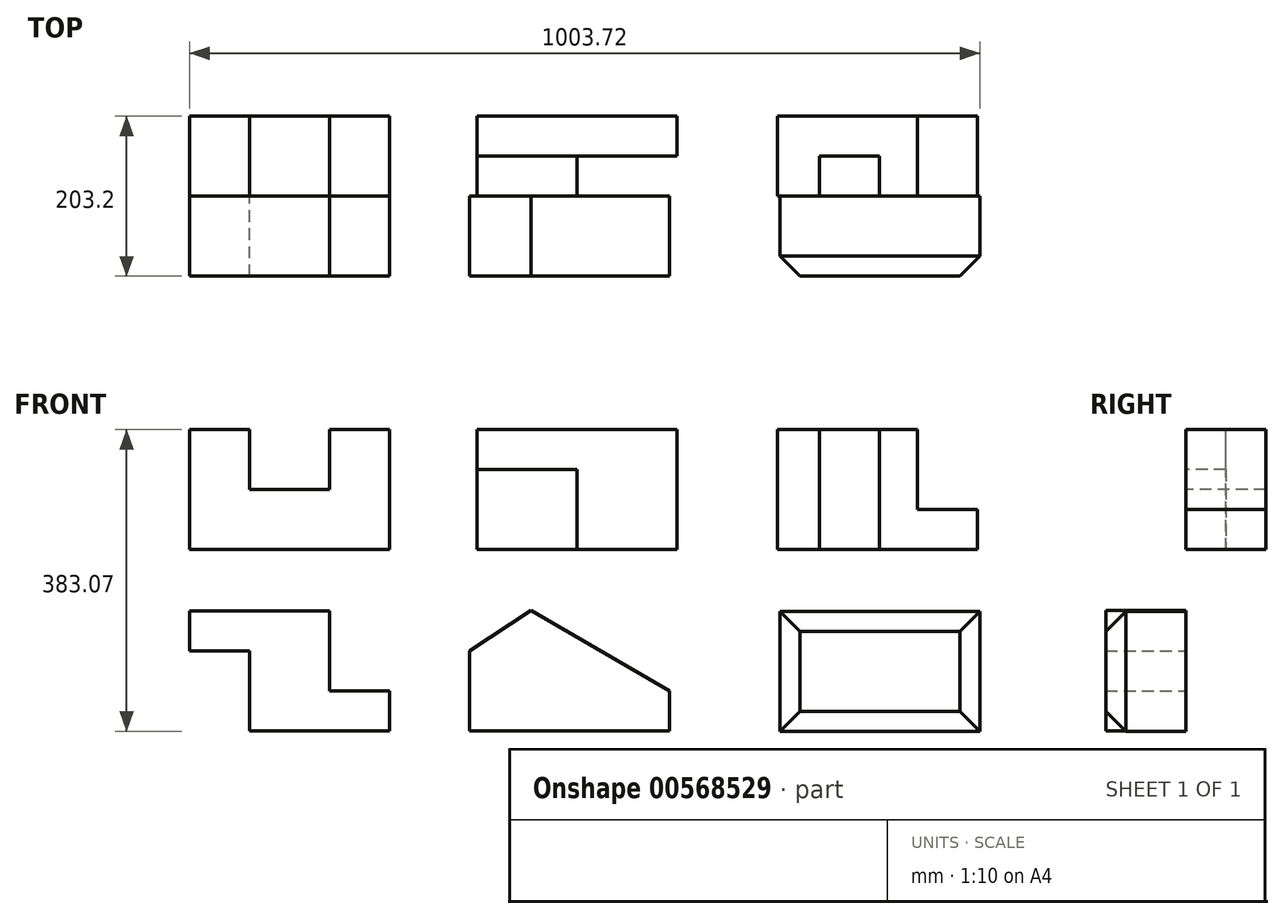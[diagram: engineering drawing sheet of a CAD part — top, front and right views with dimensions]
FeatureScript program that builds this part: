
annotation { "Feature Type Name" : "Feature", "Feature Type Description" : "" }
export const myFeature = defineFeature(function(context is Context, id is Id, definition is map)
    precondition{}
    {
        {
            var Q0;
            Q0=qCreatedBy(makeId("Front.planeOp"),FACE);
            var sketch = newSketch(context, id + "F0", { "sketchPlane" : qUnion([Q0])});
            skLineSegment(sketch, "E0", {"start": v(0, 0) * mm, "end": v(254, 0) * mm});
            skLineSegment(sketch, "E1", {"start": v(254, 0) * mm, "end": v(254, 152.4) * mm});
            skLineSegment(sketch, "E2", {"start": v(254, 152.4) * mm, "end": v(177.8, 152.4) * mm});
            skLineSegment(sketch, "E3", {"start": v(177.8, 152.4) * mm, "end": v(177.8, 76.2) * mm});
            skLineSegment(sketch, "E4", {"start": v(177.8, 76.2) * mm, "end": v(76.2, 76.2) * mm});
            skLineSegment(sketch, "E5", {"start": v(76.2, 76.2) * mm, "end": v(76.2, 152.4) * mm});
            skLineSegment(sketch, "E6", {"start": v(76.2, 152.4) * mm, "end": v(0, 152.4) * mm});
            skLineSegment(sketch, "E7", {"start": v(0, 152.4) * mm, "end": v(0, 0) * mm});
            skSolve(sketch);
        }
        {
            var Q0;
            Q0=makeQuery(id+"F0.imprint","IMPRINT",FACE,{"disambiguationData":[TD([[makeQuery(id+"F0.imprint","IMPRINT",EDGE,{"derivedFrom":sQuery(id+"F0.wireOp",EDGE,"E0")}),1.0]])]});
            extrude(context, id + "F1", {"entities" : qUnion([Q0]), "oppositeDirection" : true, "depth" : 101.6 * mm, "offsetDistance" : 25.4 * mm});
        }
        {
            var Q0;
            Q0=qCreatedBy(makeId("Front.planeOp"),FACE);
            var sketch = newSketch(context, id + "F2", { "sketchPlane" : qUnion([Q0])});
            skLineSegment(sketch, "E8.bottom", {"start": v(365.22, 0) * mm, "end": v(619.22, 0) * mm});
            skLineSegment(sketch, "E8.top", {"start": v(365.22, 152.4) * mm, "end": v(619.22, 152.4) * mm});
            skLineSegment(sketch, "E8.left", {"start": v(365.22, 0) * mm, "end": v(365.22, 152.4) * mm});
            skLineSegment(sketch, "E8.right", {"start": v(619.22, 0) * mm, "end": v(619.22, 152.4) * mm});
            skSolve(sketch);
        }
        {
            var Q0;
            Q0 = qSketchRegion(id + "F2", true);
            extrude(context, id + "F3", {"entities" : qUnion([Q0]), "oppositeDirection" : true, "depth" : 101.6 * mm, "offsetDistance" : 25.4 * mm});
        }
        {
            var Q0;
            Q0=makeQuery(id+"F3.opExtrude","CAP_FACE",FACE,{"disambiguationData":[OSD([sQuery(id+"F2.wireOp",EDGE,"E8.bottom"),sQuery(id+"F2.wireOp",EDGE,"E8.top"),sQuery(id+"F2.wireOp",EDGE,"E8.left"),sQuery(id+"F2.wireOp",EDGE,"E8.right")])],"isStart":true});
            var sketch = newSketch(context, id + "F4", { "sketchPlane" : qUnion([Q0])});
            skLineSegment(sketch, "E9", {"start": v(365.22, 101.6) * mm, "end": v(492.22, 101.6) * mm});
            skLineSegment(sketch, "E10", {"start": v(492.22, 101.6) * mm, "end": v(492.22, 0) * mm});
            skSolve(sketch);
        }
        {
            var Q0;
            {var subQ3=sQuery(id+"F4.wireOp",EDGE,"E9");Q0=makeQuery(id+"F4.imprint","IMPRINT",FACE,{"disambiguationData":[TD([[makeQuery(id+"F4.imprint","IMPRINT",EDGE,{"derivedFrom":subQ3}),1.0]])]});}
            extrude(context, id + "F5", {"entities" : qUnion([Q0]), "operationType" : NewBodyOperationType.REMOVE, "oppositeDirection" : true, "depth" : 50.8 * mm, "offsetDistance" : 25.4 * mm});
        }
        {
            var Q0;
            Q0=qCreatedBy(makeId("Front.planeOp"),FACE);
            var sketch = newSketch(context, id + "F6", { "sketchPlane" : qUnion([Q0])});
            skLineSegment(sketch, "E11", {"start": v(746.85, 0) * mm, "end": v(746.85, 152.4) * mm});
            skLineSegment(sketch, "E12", {"start": v(746.85, 152.4) * mm, "end": v(924.65, 152.4) * mm});
            skLineSegment(sketch, "E13", {"start": v(924.65, 152.4) * mm, "end": v(924.65, 50.8) * mm});
            skLineSegment(sketch, "E14", {"start": v(924.65, 50.8) * mm, "end": v(1000.85, 50.8) * mm});
            skLineSegment(sketch, "E15", {"start": v(1000.85, 50.8) * mm, "end": v(1000.85, 0) * mm});
            skLineSegment(sketch, "E16", {"start": v(1000.85, 0) * mm, "end": v(746.85, 0) * mm});
            skSolve(sketch);
        }
        {
            var Q0;
            Q0=makeQuery(id+"F6.imprint","IMPRINT",FACE,{"disambiguationData":[TD([[makeQuery(id+"F6.imprint","IMPRINT",EDGE,{"derivedFrom":sQuery(id+"F6.wireOp",EDGE,"E11")}),-1.0]])]});
            extrude(context, id + "F7", {"entities" : qUnion([Q0]), "oppositeDirection" : true, "depth" : 101.6 * mm, "offsetDistance" : 25.4 * mm});
        }
        {
            var Q0;
            Q0=makeQuery(id+"F7.opExtrude","SWEPT_FACE",FACE,{"disambiguationData":[OSD([sQuery(id+"F6.wireOp",EDGE,"E12")])]});
            var sketch = newSketch(context, id + "F8", { "sketchPlane" : qUnion([Q0])});
            skLineSegment(sketch, "E17", {"start": v(799.86, 0) * mm, "end": v(799.86, 50.8) * mm});
            skLineSegment(sketch, "E18", {"start": v(799.86, 50.8) * mm, "end": v(876.06, 50.8) * mm});
            skLineSegment(sketch, "E19", {"start": v(876.06, 50.8) * mm, "end": v(876.06, 0) * mm});
            skSolve(sketch);
        }
        {
            var Q0;
            {var subQ0=sQuery(id+"F8.wireOp",EDGE,"E17");Q0=makeQuery(id+"F8.imprint","IMPRINT",FACE,{"disambiguationData":[TD([[makeQuery(id+"F8.imprint","IMPRINT",EDGE,{"derivedFrom":subQ0}),-1.0]])]});}
            extrude(context, id + "F9", {"entities" : qUnion([Q0]), "operationType" : NewBodyOperationType.REMOVE, "oppositeDirection" : true, "depth" : 152.4 * mm, "offsetDistance" : 25.4 * mm});
        }
        {
            var Q0;
            Q0=qCreatedBy(makeId("Front.planeOp"),FACE);
            var sketch = newSketch(context, id + "F10", { "sketchPlane" : qUnion([Q0])});
            skLineSegment(sketch, "E20", {"start": v(0, -78.02) * mm, "end": v(177.8, -78.02) * mm});
            skLineSegment(sketch, "E21", {"start": v(177.8, -78.02) * mm, "end": v(177.8, -179.62) * mm});
            skLineSegment(sketch, "E22", {"start": v(177.8, -179.62) * mm, "end": v(254, -179.62) * mm});
            skLineSegment(sketch, "E23", {"start": v(254, -179.62) * mm, "end": v(254, -230.42) * mm});
            skLineSegment(sketch, "E24", {"start": v(254, -230.42) * mm, "end": v(76.2, -230.42) * mm});
            skLineSegment(sketch, "E25", {"start": v(76.2, -230.42) * mm, "end": v(76.2, -128.82) * mm});
            skLineSegment(sketch, "E26", {"start": v(76.2, -128.82) * mm, "end": v(0, -128.82) * mm});
            skLineSegment(sketch, "E27", {"start": v(0, -128.82) * mm, "end": v(0, -78.02) * mm});
            skSolve(sketch);
        }
        {
            var Q0;
            Q0=makeQuery(id+"F10.imprint","IMPRINT",FACE,{"disambiguationData":[TD([[makeQuery(id+"F10.imprint","IMPRINT",EDGE,{"derivedFrom":sQuery(id+"F10.wireOp",EDGE,"E20")}),-1.0]])]});
            extrude(context, id + "F11", {"entities" : qUnion([Q0]), "depth" : 101.6 * mm, "offsetDistance" : 25.4 * mm});
        }
        {
            var Q0;
            Q0=qCreatedBy(makeId("Front.planeOp"),FACE);
            var sketch = newSketch(context, id + "F12", { "sketchPlane" : qUnion([Q0])});
            skLineSegment(sketch, "E28", {"start": v(355.6, -230.42) * mm, "end": v(355.6, -128.82) * mm});
            skLineSegment(sketch, "E29", {"start": v(355.6, -128.82) * mm, "end": v(433.5, -77.05) * mm});
            skLineSegment(sketch, "E30", {"start": v(433.5, -77.05) * mm, "end": v(609.6, -179.62) * mm});
            skLineSegment(sketch, "E31", {"start": v(609.6, -179.62) * mm, "end": v(609.6, -230.42) * mm});
            skLineSegment(sketch, "E32", {"start": v(609.6, -230.42) * mm, "end": v(355.6, -230.42) * mm});
            skSolve(sketch);
        }
        {
            var Q0;
            Q0=makeQuery(id+"F12.imprint","IMPRINT",FACE,{"disambiguationData":[TD([[makeQuery(id+"F12.imprint","IMPRINT",EDGE,{"derivedFrom":sQuery(id+"F12.wireOp",EDGE,"E28")}),-1.0]])]});
            extrude(context, id + "F13", {"entities" : qUnion([Q0]), "depth" : 101.6 * mm, "offsetDistance" : 25.4 * mm});
        }
        {
            var Q0;
            Q0=qCreatedBy(makeId("Front.planeOp"),FACE);
            var sketch = newSketch(context, id + "F14", { "sketchPlane" : qUnion([Q0])});
            skLineSegment(sketch, "E33.bottom", {"start": v(749.72, -78.27) * mm, "end": v(1003.72, -78.27) * mm});
            skLineSegment(sketch, "E33.top", {"start": v(749.72, -230.67) * mm, "end": v(1003.72, -230.67) * mm});
            skLineSegment(sketch, "E33.left", {"start": v(749.72, -78.27) * mm, "end": v(749.72, -230.67) * mm});
            skLineSegment(sketch, "E33.right", {"start": v(1003.72, -78.27) * mm, "end": v(1003.72, -230.67) * mm});
            skSolve(sketch);
        }
        {
            var Q0;
            Q0=makeQuery(id+"F14.imprint","IMPRINT",FACE,{"disambiguationData":[TD([[makeQuery(id+"F14.imprint","IMPRINT",EDGE,{"derivedFrom":sQuery(id+"F14.wireOp",EDGE,"E33.bottom")}),-1.0]])]});
            extrude(context, id + "F15", {"entities" : qUnion([Q0]), "depth" : 101.6 * mm, "offsetDistance" : 25.4 * mm});
        }
        {
            var Q0;
            Q0=makeQuery(id+"F15.opExtrude","CAP_FACE",FACE,{"disambiguationData":[OSD([sQuery(id+"F14.wireOp",EDGE,"E33.bottom"),sQuery(id+"F14.wireOp",EDGE,"E33.top"),sQuery(id+"F14.wireOp",EDGE,"E33.left"),sQuery(id+"F14.wireOp",EDGE,"E33.right")])],"isStart":false});
            chamfer(context, id + "F16", {"entities" : qUnion([Q0]), "width" : 25.4 * mm, "tangentPropagation" : true});
        }
    });
